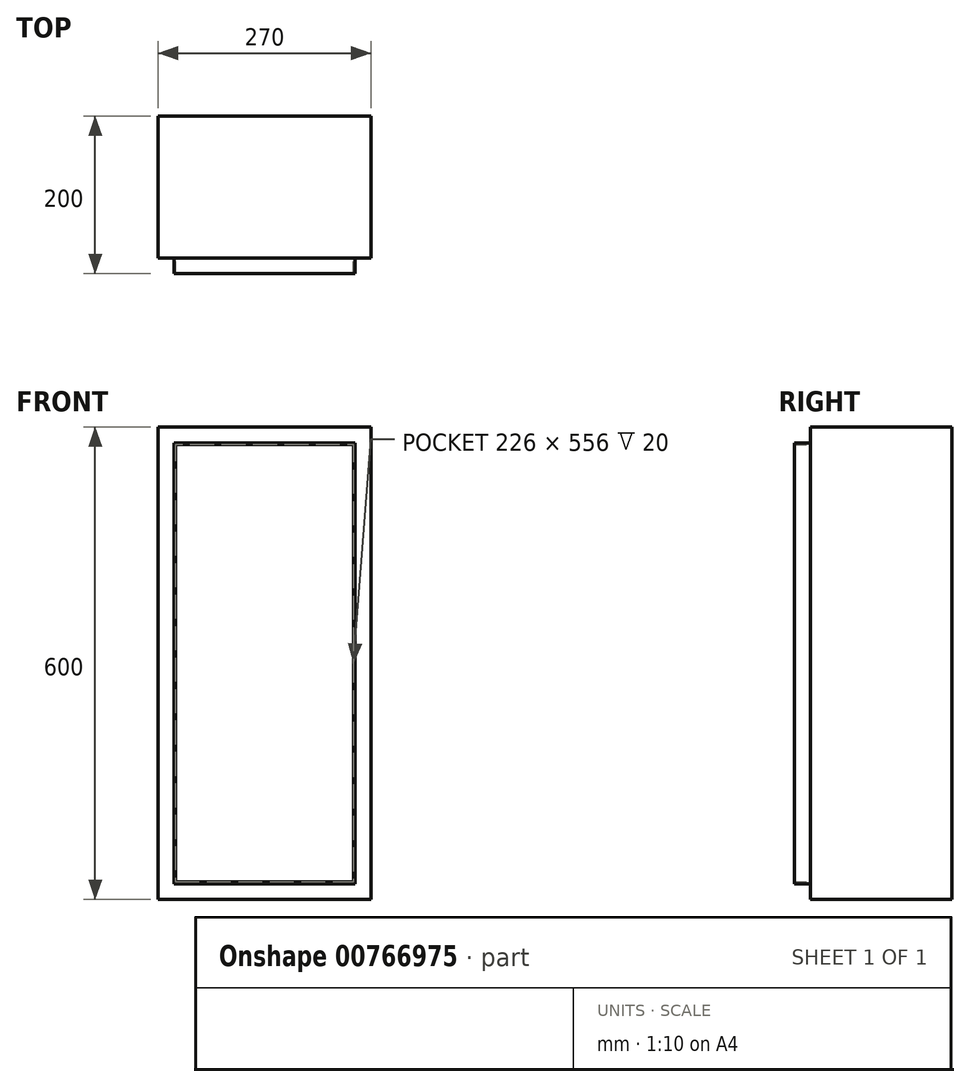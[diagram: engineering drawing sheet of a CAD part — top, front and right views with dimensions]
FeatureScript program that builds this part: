
annotation { "Feature Type Name" : "Feature", "Feature Type Description" : "" }
export const myFeature = defineFeature(function(context is Context, id is Id, definition is map)
    precondition{}
    {
        {
            var Q0;
            Q0=qCreatedBy(makeId("Front.planeOp"),FACE);
            var sketch = newSketch(context, id + "F0", { "sketchPlane" : qUnion([Q0])});
            skLineSegment(sketch, "E0", {"start": v(0, 0) * mm, "end": v(270, 0) * mm});
            skLineSegment(sketch, "E1", {"start": v(270, 0) * mm, "end": v(270, 600) * mm});
            skLineSegment(sketch, "E2", {"start": v(270, 600) * mm, "end": v(0, 600) * mm});
            skLineSegment(sketch, "E3", {"start": v(0, 600) * mm, "end": v(0, 0) * mm});
            skSolve(sketch);
        }
        {
            var Q0;
            Q0 = qSketchRegion(id + "F0", true);
            extrude(context, id + "F1", {"entities" : qUnion([Q0]), "depth" : 180 * mm, "offsetDistance" : 25 * mm});
        }
        {
            var Q0;
            Q0=makeQuery(id+"F1.opExtrude","CAP_FACE",FACE,{"disambiguationData":[OSD([sQuery(id+"F0.wireOp",EDGE,"E0"),sQuery(id+"F0.wireOp",EDGE,"E1"),sQuery(id+"F0.wireOp",EDGE,"E2"),sQuery(id+"F0.wireOp",EDGE,"E3")])],"isStart":false});
            var sketch = newSketch(context, id + "F2", { "sketchPlane" : qUnion([Q0])});
            skLineSegment(sketch, "E4", {"start": v(20, 20) * mm, "end": v(20, 580) * mm});
            skLineSegment(sketch, "E5", {"start": v(0, 600) * mm, "end": v(0, 580) * mm});
            skLineSegment(sketch, "E6", {"start": v(20, 580) * mm, "end": v(250, 580) * mm});
            skLineSegment(sketch, "E7", {"start": v(250, 580) * mm, "end": v(250, 20) * mm});
            skLineSegment(sketch, "E8", {"start": v(270, 0) * mm, "end": v(270, 20) * mm});
            skLineSegment(sketch, "E9", {"start": v(250, 20) * mm, "end": v(20, 20) * mm});
            skPoint(sketch, "E10.orphan", {"position": v(250, 0) * mm});
            skPoint(sketch, "E11.orphan", {"position": v(270, 580) * mm});
            skLineSegment(sketch, "E12.0", {"start": v(22, 578) * mm, "end": v(248, 578) * mm});
            skLineSegment(sketch, "E13.0", {"start": v(248, 22) * mm, "end": v(22, 22) * mm});
            skLineSegment(sketch, "E14.0", {"start": v(22, 22) * mm, "end": v(22, 578) * mm});
            skLineSegment(sketch, "E15.0", {"start": v(248, 578) * mm, "end": v(248, 22) * mm});
            skSolve(sketch);
        }
        {
            var Q0;
            Q0 = qSketchRegion(id + "F2", true);
            extrude(context, id + "F3", {"entities" : qUnion([Q0]), "operationType" : NewBodyOperationType.ADD, "depth" : 20 * mm, "offsetDistance" : 25 * mm});
        }
    });
